# Revit family: Hager-WITTY PLUS WALL MOUNTED-nl-BE-BE
name_source: partatom
category: Electrical Fixtures
units: mm (PartAtom-declared; Revit-internal decimal feet)

## family parameters
Always vertical = Yes
Cut with Voids When Loaded = No
Host = Wall
Maintain Annotation Orientation = No
OmniClass Number = 23.75.00.00
OmniClass Title = Climate Control (HVAC)
Part Type = Normal
Room Calculation Point = No
Round Connector Dimension = Use Diameter
Shared = No

## types (4) — shared parameters
BC_METADATA = {"ObjectGuid":"b7395028-ef9e-46b8-b49f-e0fe9c8fa070","ModelGuid":"b1efb829-c177-4a88-8b0d-f632edc25d22","VariantGuid":"c7b0c534-fef0-4725-a2d6-e8a658ebdb92","Revision":"#2","VariantName":"REF 1"}
BC_MODEL_ID = 1528867
BC_OBJECT_ID = 511138
BC_OBJECT_VERSION = #1
Code hager = ADD_EC002883_ECVS_WO
EF000003 - Montagewijze = Wandmontage
EF000008 - Breedte = 250 mm  [stored 0.82021 ft]
EF000040 - Hoogte = 370 mm  [stored 1.21391 ft]
EF000049 - Diepte = 150 mm  [stored 0.492126 ft]
EF000458 - Met display = No
EF001596 - Materiaal behuizing = Kunststof
EF002136 - Nominaal aansluitvermogen = 22000 W
EF003840 - Ingangsspanning = 400 V
EF004293 - Slagvastheid = IK10
EF005455 - Frequentie = 50/60 Hz
EF005474 - Beschermingsgraad (IP) = IP55
EF007001 - Uitgangsspanning bij DC = 0 V
EF007353 - Maxi. uitgangsstroom bij DC = 0 A
EF009078 - Aantal laadpunten = 1
EF009089 - Met huishoudelijke aansluitkast (HAK) = No
EF009300 - Max. vermogen per laadpunt = 22000 W
EF009313 - Met energieteller, energiemeter = Yes
EF009314 - Met vermogenschakelaar = No
EF009547 - LTE = No
EF011072 - Met IFTTT ondersteuning = No
EF012191 - Met ingebouwde RFID-kaartlezer = Yes
EF012361 - NFC (Near Field Communication) = No
EF013154 - Verbinding via WLAN = Yes
EF014925 - Compatible met Apple HomeKit = No
EF014926 - Compatible met Google Assistant = No
EF014927 - Compatible met Amazon Alexa = No
EF016385 - Mobiele communicatiestandaard 5G = No
EF017508 - Geschikt voor netwerken als master = No
EF017509 - DC reststroomdetectie = No
EF017510 - Lasdetectie van schakelaars = No
EF017511 - Met sleutelschakelaar = No
EF017512 - Export van oplaadlogs = Yes
EF017513 - Open Charge Point Protocol (OCPP) versie = 1.6
EF017515 - Plug and charge (ISO 15118) = No
EF017517 - Geschikt voor netwerken als uitbreiding = No
EF017663 - Laadkabel permanent vergrendelbaar op laadapparaat = No
EF017664 - In netwerk op te nemen via LAN = Yes
EF017665 - Met MID-compatibele energiemeter = Yes
EF017669 - Geschikt voor dynamisch belastingmanagement = Yes
EF017672 - Backend meegeleverd = No
EF017972 - Bediening en configuratie per app = Yes
EF025053 - Uitvoering aansluiting installatiezijde = 3-fasig
EFDE0066 - Conform de kalibratiewet = No
ETIM class code = EC002883
ETIM class name = Charging device E-Mobility
HG000003-Range = WITTY PLUS
HG000065-With socket TE = No
HG000099-Onfly Template ID = WittyOne_EVCS_Wall_Mounted
Manufacturer = hager France
Name = WITTY PLUS WALL MOUNTED-BE
Name BIM&CO = Electricity
Name hager = ADD_ChargingStation_EC002883
Reference description = ECVS Witty 1x22kW 3P T2S
zero-valued in all types: Default Elevation, EF008200 - Aansluitbare geleiderdoorsnede, EF009091 - Aantal FI-schakelaars type A, EF009092 - Aantal FI-schakelaars type B, EF009301 - Aantal oplaadkoppelingen type 1, EF009302 - Aantal oplaadkoppelingen type 1 CCS, EF009303 - Aantal oplaadkoppelingen type 2, EF009304 - Aantal oplaadkoppelingen type 2 CCS, EF009306 - Aantal oplaadkoppelingen type GB AC, EF009307 - Aantal oplaadkoppelingen type GB DC, EF009310 - Aantal oplaadkoppelingen CHAdeMO, EF009311 - Aantal huishoudelijke stopcontacten

## per-type parameters (varying)
| type | BC_VARIANT_ID | EF014895 - Lengte van de laadkabel | EF017668 - Statisch belastingmanagement geïntegreerd | HG000004-Manufacturer reference |
| WITTY PLUS-1x22kW-3P-XVL122SPI-WALL MOUNTED | 1164645 | 0 mm  [stored 0 ft] | Yes | XVL122SPI |
| WITTY PLUS-1x22kW-3P-XVL122C-WALL MOUNTED | 1164646 | 6500 mm  [stored 21.3255 ft] | No | XVL122C |
| WITTY PLUS-1x22kW-3P-XVL122S-WALL MOUNTED | 1164647 | 0 mm  [stored 0 ft] | No | XVL122S |
| WITTY PLUS-1x22kW-3P-XVL122CPI-WALL MOUNTED | 1164648 | 6500 mm  [stored 21.3255 ft] | Yes | XVL122CPI |

note: column(s) folded — value = type name in every type: Reference

note: [stored X ft] marks values corroborated as IEEE doubles in the binary element streams (Revit-internal decimal feet)
